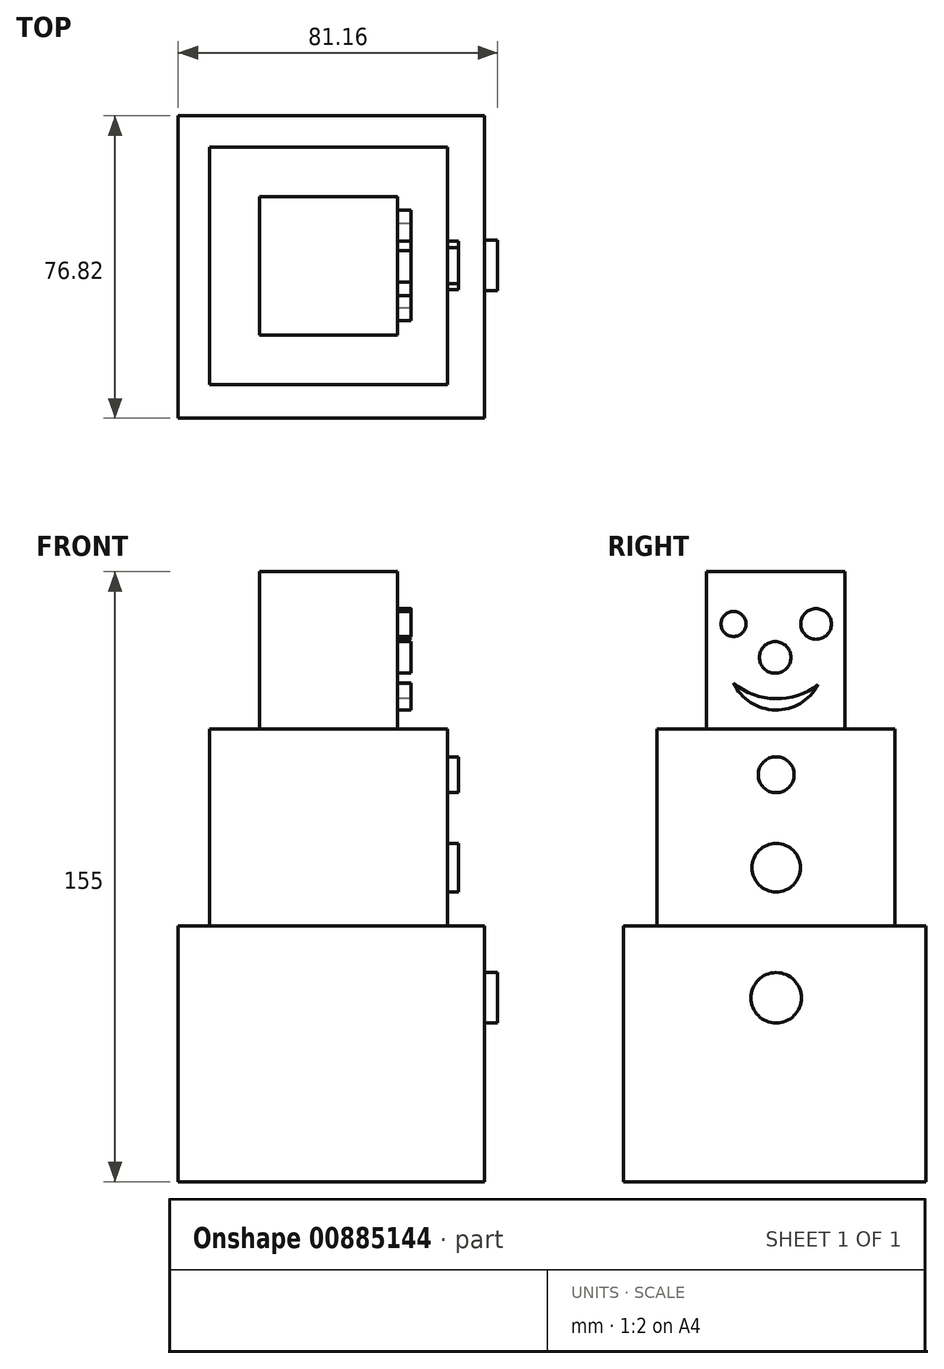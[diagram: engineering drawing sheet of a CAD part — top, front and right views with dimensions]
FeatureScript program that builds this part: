
annotation { "Feature Type Name" : "Feature", "Feature Type Description" : "" }
export const myFeature = defineFeature(function(context is Context, id is Id, definition is map)
    precondition{}
    {
        {
            var Q0;
            Q0=qCreatedBy(makeId("Top.planeOp"),FACE);
            var sketch = newSketch(context, id + "F0", { "sketchPlane" : qUnion([Q0])});
            skLineSegment(sketch, "E0", {"start": v(-41.45, -27.92) * mm, "end": v(-41.45, 48.9) * mm});
            skLineSegment(sketch, "E1", {"start": v(-41.45, 48.9) * mm, "end": v(36.33, 48.9) * mm});
            skLineSegment(sketch, "E2", {"start": v(36.33, 48.9) * mm, "end": v(36.33, -27.92) * mm});
            skLineSegment(sketch, "E3", {"start": v(36.33, -27.92) * mm, "end": v(-41.45, -27.92) * mm});
            skSolve(sketch);
        }
        {
            var Q0;
            Q0 = qSketchRegion(id + "F0", true);
            extrude(context, id + "F1", {"entities" : qUnion([Q0]), "depth" : 65 * mm, "offsetDistance" : 25.4 * mm});
        }
        {
            var Q0;
            Q0=makeQuery(id+"F1.opExtrude","CAP_FACE",FACE,{"disambiguationData":[OSD([sQuery(id+"F0.wireOp",EDGE,"E0"),sQuery(id+"F0.wireOp",EDGE,"E1"),sQuery(id+"F0.wireOp",EDGE,"E2"),sQuery(id+"F0.wireOp",EDGE,"E3")])],"isStart":false});
            var sketch = newSketch(context, id + "F2", { "sketchPlane" : qUnion([Q0])});
            skLineSegment(sketch, "E4.bottom", {"start": v(-33.47, 40.94) * mm, "end": v(26.93, 40.94) * mm});
            skLineSegment(sketch, "E4.top", {"start": v(-33.47, -19.46) * mm, "end": v(26.93, -19.46) * mm});
            skLineSegment(sketch, "E4.left", {"start": v(-33.47, 40.94) * mm, "end": v(-33.47, -19.46) * mm});
            skLineSegment(sketch, "E4.right", {"start": v(26.93, 40.94) * mm, "end": v(26.93, -19.46) * mm});
            skSolve(sketch);
        }
        {
            var Q0;
            Q0 = qSketchRegion(id + "F2", true);
            extrude(context, id + "F3", {"entities" : qUnion([Q0]), "operationType" : NewBodyOperationType.ADD, "depth" : 50 * mm, "offsetDistance" : 25.4 * mm});
        }
        {
            var Q0;
            Q0=makeQuery(id+"F3.opExtrude","CAP_FACE",FACE,{"disambiguationData":[OSD([sQuery(id+"F2.wireOp",EDGE,"E4.bottom"),sQuery(id+"F2.wireOp",EDGE,"E4.top"),sQuery(id+"F2.wireOp",EDGE,"E4.left"),sQuery(id+"F2.wireOp",EDGE,"E4.right")])],"isStart":false});
            var sketch = newSketch(context, id + "F4", { "sketchPlane" : qUnion([Q0])});
            skLineSegment(sketch, "E5.bottom", {"start": v(-20.85, 28.32) * mm, "end": v(14.31, 28.32) * mm});
            skLineSegment(sketch, "E5.top", {"start": v(-20.85, -6.84) * mm, "end": v(14.31, -6.84) * mm});
            skLineSegment(sketch, "E5.left", {"start": v(-20.85, 28.32) * mm, "end": v(-20.85, -6.84) * mm});
            skLineSegment(sketch, "E5.right", {"start": v(14.31, 28.32) * mm, "end": v(14.31, -6.84) * mm});
            skPoint(sketch, "E5.middle", {"position": v(-3.27, 10.74) * mm});
            skPoint(sketch, "E5.middle.positionSnap0", {"position": v(-3.27, 40.94) * mm});
            skPoint(sketch, "E5.middle.positionSnap1", {"position": v(-33.47, 10.74) * mm});
            skPoint(sketch, "E5.centerSnap0", {"position": v(-3.27, 40.94) * mm});
            skPoint(sketch, "E5.centerSnap1", {"position": v(-33.47, 10.74) * mm});
            skSolve(sketch);
        }
        {
            var Q0;
            Q0 = qSketchRegion(id + "F4", true);
            extrude(context, id + "F5", {"entities" : qUnion([Q0]), "operationType" : NewBodyOperationType.ADD, "depth" : 40 * mm, "offsetDistance" : 25.4 * mm});
        }
        {
            var Q0;
            Q0=makeQuery(id+"F5.opExtrude","SWEPT_FACE",FACE,{"disambiguationData":[OSD([sQuery(id+"F4.wireOp",EDGE,"E5.right")])]});
            var sketch = newSketch(context, id + "F6", { "sketchPlane" : qUnion([Q0])});
            skCircle(sketch, "E6", {"center": v(0, 141.7) * mm, "radius": 3.17 * mm});
            skCircle(sketch, "E7", {"center": v(20.97, 141.7) * mm, "radius": 3.9 * mm});
            skCircle(sketch, "E8", {"center": v(10.58, 133.2) * mm, "radius": 4 * mm});
            skArc(sketch, "E9", {"start": v(0, 126.68) * mm, "mid": v(10.6, 119.84) * mm, "end": v(21.46, 126.29) * mm});
            skArc(sketch, "E10", {"start": v(0, 126.68) * mm, "mid": v(10.66, 122.72) * mm, "end": v(21.46, 126.29) * mm});
            skCircle(sketch, "E11", {"center": v(10.83, 103.4) * mm, "radius": 4.56 * mm});
            skCircle(sketch, "E12", {"center": v(10.83, 79.78) * mm, "radius": 6.15 * mm});
            skCircle(sketch, "E13", {"center": v(10.83, 46.72) * mm, "radius": 6.4 * mm});
            skSolve(sketch);
        }
        {
            var Q0;
            Q0 = qSketchRegion(id + "F6", true);
            extrude(context, id + "F7", {"entities" : qUnion([Q0]), "operationType" : NewBodyOperationType.ADD, "depth" : 25.4 * mm, "offsetDistance" : 25.4 * mm});
        }
        {
            var Q0;
            Q0=makeQuery(id+"F7.opExtrude","CAP_FACE",FACE,{"disambiguationData":[OSD([sQuery(id+"F6.wireOp",EDGE,"E12")])],"isStart":false});
            var sketch = newSketch(context, id + "F8", { "sketchPlane" : qUnion([Q0])});
            skCircle(sketch, "E14.0.0", {"center": v(10.83, 103.4) * mm, "radius": 4.56 * mm});
            skArc(sketch, "E15.0.0", {"start": v(21.46, 126.29) * mm, "mid": v(10.66, 122.72) * mm, "end": v(0, 126.68) * mm});
            skArc(sketch, "E15.0.1", {"start": v(0, 126.68) * mm, "mid": v(10.6, 119.84) * mm, "end": v(21.46, 126.29) * mm});
            skCircle(sketch, "E16.0", {"center": v(10.83, 79.78) * mm, "radius": 6.15 * mm});
            skCircle(sketch, "E17.0", {"center": v(10.58, 133.2) * mm, "radius": 4 * mm});
            skCircle(sketch, "E18.0", {"center": v(20.97, 141.7) * mm, "radius": 3.9 * mm});
            skCircle(sketch, "E19.0", {"center": v(0, 141.7) * mm, "radius": 3.17 * mm});
            skSolve(sketch);
        }
        {
            var Q0;
            Q0 = qSketchRegion(id + "F8", true);
            extrude(context, id + "F9", {"entities" : qUnion([Q0]), "operationType" : NewBodyOperationType.REMOVE, "oppositeDirection" : true, "depth" : 10 * mm, "offsetDistance" : 25.4 * mm});
        }
        {
            var Q0;
            Q0=makeQuery(id+"F9.boolean.opBoolean","COPY",FACE,{"derivedFrom":makeQuery(id+"F9.opExtrude","CAP_FACE",FACE,{"disambiguationData":[OSD([sQuery(id+"F8.wireOp",EDGE,"E19.0")])],"isStart":false})});
            var sketch = newSketch(context, id + "F10", { "sketchPlane" : qUnion([Q0])});
            skCircle(sketch, "E20.0", {"center": v(0, 141.7) * mm, "radius": 3.17 * mm});
            skCircle(sketch, "E21.0", {"center": v(10.58, 133.2) * mm, "radius": 4 * mm});
            skCircle(sketch, "E22.0", {"center": v(20.97, 141.7) * mm, "radius": 3.9 * mm});
            skArc(sketch, "E23.0", {"start": v(21.46, 126.29) * mm, "mid": v(10.66, 122.72) * mm, "end": v(0, 126.68) * mm});
            skArc(sketch, "E24.0", {"start": v(0, 126.68) * mm, "mid": v(10.6, 119.84) * mm, "end": v(21.46, 126.29) * mm});
            skSolve(sketch);
        }
        {
            var Q0;
            Q0 = qSketchRegion(id + "F10", true);
            extrude(context, id + "F11", {"entities" : qUnion([Q0]), "operationType" : NewBodyOperationType.REMOVE, "oppositeDirection" : true, "depth" : 12 * mm, "offsetDistance" : 25.4 * mm});
        }
    });
